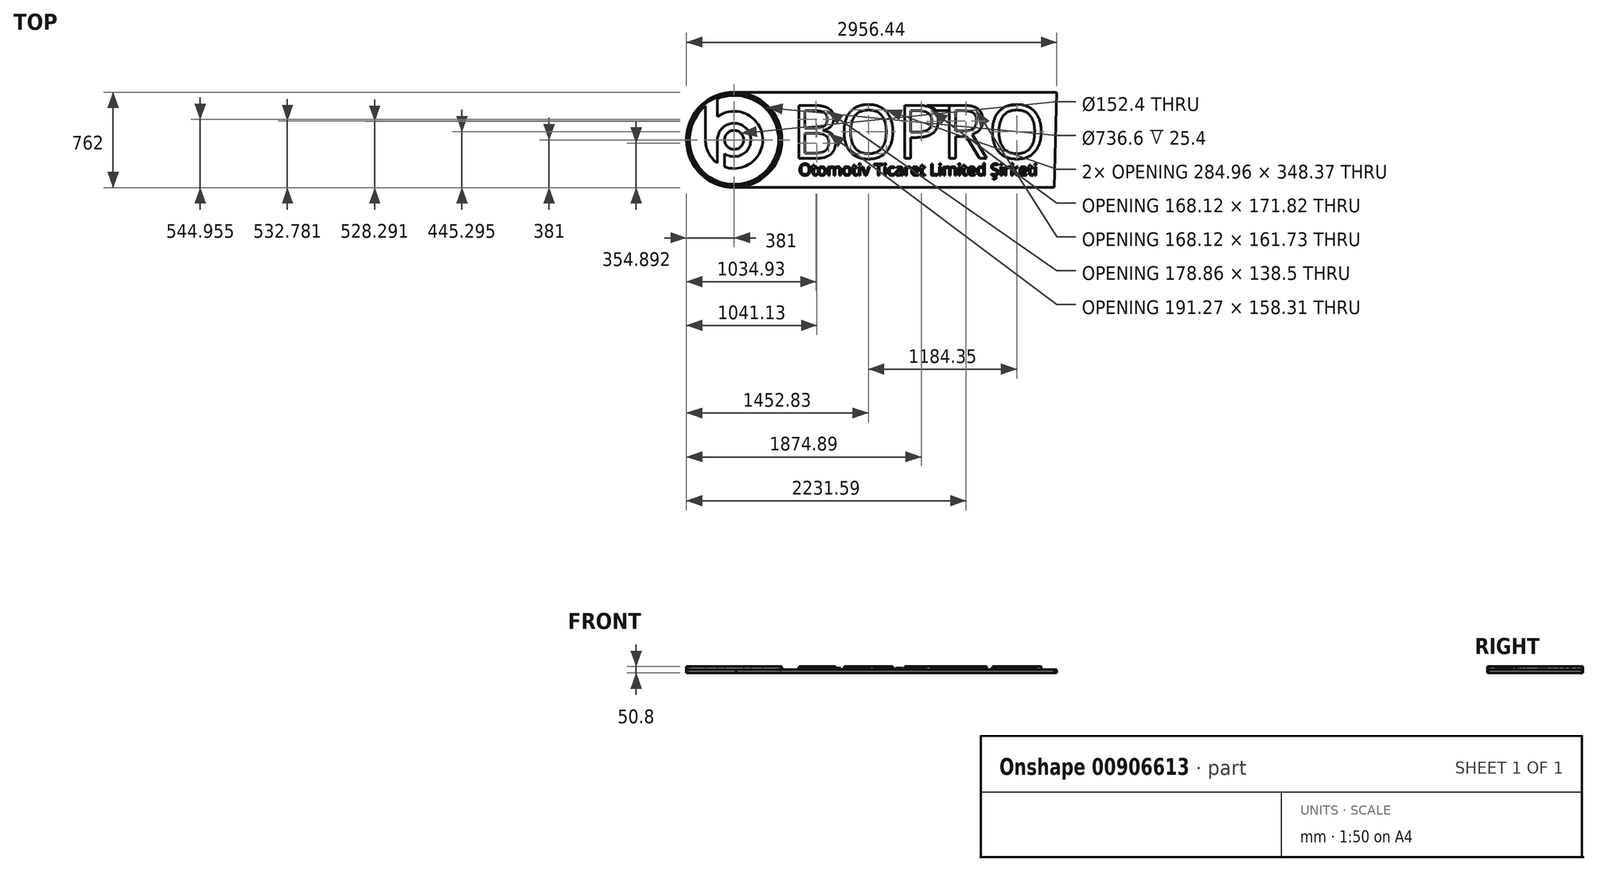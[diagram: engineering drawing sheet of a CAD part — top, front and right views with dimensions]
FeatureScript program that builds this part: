
annotation { "Feature Type Name" : "Feature", "Feature Type Description" : "" }
export const myFeature = defineFeature(function(context is Context, id is Id, definition is map)
    precondition{}
    {
        {
            var Q0;
            Q0=qCreatedBy(makeId("Top.planeOp"),FACE);
            var sketch = newSketch(context, id + "F0", { "sketchPlane" : qUnion([Q0])});
            skCircle(sketch, "E0", {"center": v(0, 0) * mm, "radius": 76.2 * mm});
            skArc(sketch, "E1", {"start": v(-76.2, -109.43) * mm, "mid": v(118.2, 61.73) * mm, "end": v(-133.35, 0) * mm});
            skArc(sketch, "E2", {"start": v(-228.6, 0) * mm, "mid": v(-203.4, -104.34) * mm, "end": v(-133.35, -185.68) * mm});
            skArc(sketch, "E3", {"start": v(-228.6, 272.38) * mm, "mid": v(183.23, -304.76) * mm, "end": v(-133.35, 329.65) * mm});
            skCircle(sketch, "E4", {"center": v(0, 0) * mm, "radius": 368.3 * mm});
            skCircle(sketch, "E5", {"center": v(0, 0) * mm, "radius": 381 * mm});
            skLineSegment(sketch, "E6", {"start": v(-76.2, -109.43) * mm, "end": v(-76.2, -215.53) * mm});
            skLineSegment(sketch, "E7", {"start": v(-133.35, 0) * mm, "end": v(-133.35, -185.68) * mm});
            skPoint(sketch, "E8.orphan", {"position": v(-76.2, 0) * mm});
            skLineSegment(sketch, "E9", {"start": v(-228.6, 0) * mm, "end": v(-228.6, 272.38) * mm});
            skLineSegment(sketch, "E10", {"start": v(-133.35, 185.68) * mm, "end": v(-133.35, 329.65) * mm});
            skArc(sketch, "E11.trimOffspring", {"start": v(-76.2, -215.53) * mm, "mid": v(226.32, 32.24) * mm, "end": v(-133.35, 185.68) * mm});
            skSolve(sketch);
        }
        {
            var Q0;
            Q0=makeQuery(id+"F0.imprint","IMPRINT",FACE,{"disambiguationData":[TD([[makeQuery(id+"F0.imprint","IMPRINT",EDGE,{"derivedFrom":sQuery(id+"F0.wireOp",EDGE,"E4")}),-1.0]])]});
            var Q1;
            Q1=makeQuery(id+"F0.imprint","IMPRINT",FACE,{"disambiguationData":[TD([[makeQuery(id+"F0.imprint","IMPRINT",EDGE,{"derivedFrom":sQuery(id+"F0.wireOp",EDGE,"E1")}),-1.0]])]});
            var Q2;
            Q2=makeQuery(id+"F0.imprint","IMPRINT",FACE,{"disambiguationData":[TD([[makeQuery(id+"F0.imprint","IMPRINT",EDGE,{"derivedFrom":sQuery(id+"F0.wireOp",EDGE,"E0")}),-1.0]])]});
            var Q3;
            Q3=makeQuery(id+"F0.imprint","IMPRINT",FACE,{"disambiguationData":[TD([[makeQuery(id+"F0.imprint","IMPRINT",EDGE,{"derivedFrom":sQuery(id+"F0.wireOp",EDGE,"E0")}),1.0]])]});
            extrude(context, id + "F1", {"entities" : qUnion([Q0, Q1, Q2, Q3]), "oppositeDirection" : true, "depth" : 25.4 * mm, "offsetDistance" : 25.4 * mm});
        }
        {
            var Q0;
            Q0=makeQuery(id+"F0.imprint","IMPRINT",FACE,{"disambiguationData":[TD([[makeQuery(id+"F0.imprint","IMPRINT",EDGE,{"derivedFrom":sQuery(id+"F0.wireOp",EDGE,"E4")}),-1.0]])]});
            var Q1;
            Q1=makeQuery(id+"F0.imprint","IMPRINT",FACE,{"disambiguationData":[TD([[makeQuery(id+"F0.imprint","IMPRINT",EDGE,{"derivedFrom":sQuery(id+"F0.wireOp",EDGE,"E0")}),-1.0]])]});
            extrude(context, id + "F2", {"entities" : qUnion([Q0, Q1]), "depth" : 25.4 * mm, "offsetDistance" : 25.4 * mm});
        }
        {
            var Q0;
            Q0=makeQuery(id+"F1.opExtrude","CAP_FACE",FACE,{"disambiguationData":[OSD([sQuery(id+"F0.wireOp",EDGE,"E5")])],"isStart":false});
            var sketch = newSketch(context, id + "F3", { "sketchPlane" : qUnion([Q0])});
            skCircle(sketch, "E12", {"center": v(0, 0) * mm, "radius": 368.3 * mm});
            skSolve(sketch);
        }
        {
            var Q0;
            Q0=makeQuery(id+"F3.imprint","IMPRINT",FACE,{"disambiguationData":[TD([[makeQuery(id+"F3.imprint","IMPRINT",EDGE,{"derivedFrom":sQuery(id+"F3.wireOp",EDGE,"E12")}),-1.0]])]});
            extrude(context, id + "F4", {"entities" : qUnion([Q0]), "operationType" : NewBodyOperationType.REMOVE, "oppositeDirection" : true, "depth" : 25.4 * mm, "offsetDistance" : 25.4 * mm});
        }
        {
            var Q0;
            Q0=makeQuery(id+"F1.opExtrude","CAP_FACE",FACE,{"disambiguationData":[OSD([sQuery(id+"F0.wireOp",EDGE,"E5")])],"isStart":true});
            var sketch = newSketch(context, id + "F5", { "sketchPlane" : qUnion([Q0])});
            skCircle(sketch, "E13.0", {"center": v(0, 0) * mm, "radius": 381 * mm});
            skLineSegment(sketch, "E14", {"start": v(-0.13, 381) * mm, "end": v(2575.44, 381) * mm});
            skLineSegment(sketch, "E15", {"start": v(14.68, -380.72) * mm, "end": v(2554.68, -380.72) * mm});
            skLineSegment(sketch, "E16", {"start": v(2575.44, 381) * mm, "end": v(2554.68, -380.72) * mm});
            skSolve(sketch);
        }
        {
            var Q0;
            Q0 = qSketchRegion(id + "F5", true);
            extrude(context, id + "F6", {"entities" : qUnion([Q0]), "oppositeDirection" : true, "depth" : 25.4 * mm, "offsetDistance" : 25.4 * mm});
        }
        {
            var Q0;
            Q0=makeQuery(id+"F6.opExtrude","CAP_FACE",FACE,{"disambiguationData":[OSD([sQuery(id+"F5.wireOp",EDGE,"E13.0"),sQuery(id+"F5.wireOp",EDGE,"E14"),sQuery(id+"F5.wireOp",EDGE,"E15"),sQuery(id+"F5.wireOp",EDGE,"E16")])],"isStart":true});
            var sketch = newSketch(context, id + "F7", { "sketchPlane" : qUnion([Q0])});
            skText(sketch, "E17", { "text": "BOPRO", "fontName": "OpenSans-Regular.ttf"});
            skCircle(sketch, "E18.0", {"center": v(0, 0) * mm, "radius": 381 * mm});
            skLineSegment(sketch, "E19.0.0", {"start": v(2575.44, 381) * mm, "end": v(0.13, 381) * mm});
            skArc(sketch, "E19.0.1", {"start": v(0.13, 381) * mm, "mid": v(-380.93, -7.27) * mm, "end": v(14.68, -380.72) * mm});
            skLineSegment(sketch, "E19.0.2", {"start": v(14.68, -380.72) * mm, "end": v(2554.68, -380.72) * mm});
            skLineSegment(sketch, "E19.0.3", {"start": v(2554.68, -380.72) * mm, "end": v(2575.44, 381) * mm});
            const initialGuessF7  = {"E17": [0.4572, -0.1472, 1, 0, 0.4266]};
            skSetInitialGuess(sketch, initialGuessF7);
            skSolve(sketch);
        }
        {
            var Q0;
            Q0=makeQuery(id+"F7.imprint","IMPRINT",FACE,{"disambiguationData":[TD([[makeQuery(id+"F7.imprint","IMPRINT",EDGE,{"derivedFrom":sQuery(id+"F7.wireOp",EDGE,"E17.sketch_text.stroke-0")}),-1.0]])]});
            var Q1;
            Q1=makeQuery(id+"F7.imprint","IMPRINT",FACE,{"disambiguationData":[TD([[makeQuery(id+"F7.imprint","IMPRINT",EDGE,{"derivedFrom":sQuery(id+"F7.wireOp",EDGE,"E17.sketch_text.stroke-25")}),-1.0]])]});
            var Q2;
            Q2=makeQuery(id+"F7.imprint","IMPRINT",FACE,{"disambiguationData":[TD([[makeQuery(id+"F7.imprint","IMPRINT",EDGE,{"derivedFrom":sQuery(id+"F7.wireOp",EDGE,"E17.sketch_text.stroke-41")}),-1.0]])]});
            var Q3;
            Q3=makeQuery(id+"F7.imprint","IMPRINT",FACE,{"disambiguationData":[TD([[makeQuery(id+"F7.imprint","IMPRINT",EDGE,{"derivedFrom":sQuery(id+"F7.wireOp",EDGE,"E17.sketch_text.stroke-56")}),-1.0]])]});
            var Q4;
            Q4=makeQuery(id+"F7.imprint","IMPRINT",FACE,{"disambiguationData":[TD([[makeQuery(id+"F7.imprint","IMPRINT",EDGE,{"derivedFrom":sQuery(id+"F7.wireOp",EDGE,"E17.sketch_text.stroke-74")}),-1.0]])]});
            extrude(context, id + "F8", {"entities" : qUnion([Q0, Q1, Q2, Q3, Q4]), "depth" : 25.4 * mm, "offsetDistance" : 25.4 * mm});
        }
        {
            var Q0;
            Q0=makeQuery(id+"F8.opExtrude","CAP_FACE",FACE,{"disambiguationData":[OSD([sQuery(id+"F7.wireOp",EDGE,"E17.sketch_text.stroke-56"),sQuery(id+"F7.wireOp",EDGE,"E17.sketch_text.stroke-57"),sQuery(id+"F7.wireOp",EDGE,"E17.sketch_text.stroke-58"),sQuery(id+"F7.wireOp",EDGE,"E17.sketch_text.stroke-59"),sQuery(id+"F7.wireOp",EDGE,"E17.sketch_text.stroke-60"),sQuery(id+"F7.wireOp",EDGE,"E17.sketch_text.stroke-61"),sQuery(id+"F7.wireOp",EDGE,"E17.sketch_text.stroke-62"),sQuery(id+"F7.wireOp",EDGE,"E17.sketch_text.stroke-63"),sQuery(id+"F7.wireOp",EDGE,"E17.sketch_text.stroke-64"),sQuery(id+"F7.wireOp",EDGE,"E17.sketch_text.stroke-65"),sQuery(id+"F7.wireOp",EDGE,"E17.sketch_text.stroke-66"),sQuery(id+"F7.wireOp",EDGE,"E17.sketch_text.stroke-67"),sQuery(id+"F7.wireOp",EDGE,"E17.sketch_text.stroke-68"),sQuery(id+"F7.wireOp",EDGE,"E17.sketch_text.stroke-69"),sQuery(id+"F7.wireOp",EDGE,"E17.sketch_text.stroke-70"),sQuery(id+"F7.wireOp",EDGE,"E17.sketch_text.stroke-71"),sQuery(id+"F7.wireOp",EDGE,"E17.sketch_text.stroke-72"),sQuery(id+"F7.wireOp",EDGE,"E17.sketch_text.stroke-73")])],"isStart":false});
            var sketch = newSketch(context, id + "F9", { "sketchPlane" : qUnion([Q0])});
            skLineSegment(sketch, "E20.0.1", {"start": v(1854.85, 28.7) * mm, "end": v(1957.25, -147.2) * mm});
            skLineSegment(sketch, "E20.0.2", {"start": v(1957.25, -147.2) * mm, "end": v(2015.38, -147.2) * mm});
            skLineSegment(sketch, "E20.0.3", {"start": v(2015.38, -147.2) * mm, "end": v(1900.5, 42.86) * mm});
            skFitSpline(sketch, "E20.0.4", {"points": [v(1900.5, 42.86) * mm, v(1985.57, 72.4) * mm, v(1985.57, 156.27) * mm]});
            skFitSpline(sketch, "E20.0.5", {"points": [v(1985.57, 156.27) * mm, v(1985.57, 216.17) * mm, v(1948.4, 245.98) * mm]});
            skFitSpline(sketch, "E20.0.6", {"points": [v(1948.4, 245.98) * mm, v(1911.23, 275.79) * mm, v(1833.38, 275.79) * mm]});
            skLineSegment(sketch, "E20.0.7", {"start": v(1833.38, 275.79) * mm, "end": v(1717.38, 275.79) * mm});
            skFitSpline(sketch, "E21.0.0", {"points": [v(1628.87, 152.57) * mm, v(1628.87, 275.79) * mm, v(1470.38, 275.79) * mm]});
            skLineSegment(sketch, "E21.0.1", {"start": v(1470.38, 275.79) * mm, "end": v(1360.67, 275.79) * mm});
            skLineSegment(sketch, "E21.0.2", {"start": v(1360.67, 275.79) * mm, "end": v(1360.67, -147.2) * mm});
            skLineSegment(sketch, "E21.0.3", {"start": v(1360.67, -147.2) * mm, "end": v(1409.83, -147.2) * mm});
            skLineSegment(sketch, "E21.0.4", {"start": v(1409.83, -147.2) * mm, "end": v(1409.83, 19.16) * mm});
            skLineSegment(sketch, "E21.0.5", {"start": v(1409.83, 19.16) * mm, "end": v(1459.64, 19.16) * mm});
            skFitSpline(sketch, "E21.0.6", {"points": [v(1459.64, 19.16) * mm, v(1541.2, 19.16) * mm, v(1585.03, 53.74) * mm]});
            skFitSpline(sketch, "E21.0.7", {"points": [v(1585.03, 53.74) * mm, v(1628.87, 88.32) * mm, v(1628.87, 152.57) * mm]});
            skLineSegment(sketch, "E22", {"start": v(1717.38, 275.79) * mm, "end": v(1540.02, 275.79) * mm});
            skLineSegment(sketch, "E23", {"start": v(1766.53, 232.65) * mm, "end": v(1612.47, 232.65) * mm});
            skFitSpline(sketch, "E24", {"points": [v(1540.02, 275.79) * mm, v(1579.9, 261.04) * mm, v(1612.47, 232.65) * mm], "startDerivative": vector(63.64, -12.57) * mm, "endDerivative": vector(28.33, -37.92) * mm});
            skLineSegment(sketch, "E25", {"start": v(1957.25, -147.2) * mm, "end": v(1830.28, 70.91) * mm});
            skPoint(sketch, "E20.0.10.end.orphan", {"position": v(1766.53, 28.7) * mm});
            skPoint(sketch, "E20.0.9.end.orphan", {"position": v(1766.53, -147.2) * mm});
            skPoint(sketch, "E20.0.9.start.orphan", {"position": v(1717.38, -147.2) * mm});
            skSolve(sketch);
        }
        {
            var Q0;
            {var subQ0=sQuery(id+"F9.wireOp",EDGE,"E22");Q0=makeQuery(id+"F9.imprint","IMPRINT",FACE,{"disambiguationData":[TD([[makeQuery(id+"F9.imprint","IMPRINT",EDGE,{"derivedFrom":subQ0}),1.0]])]});}
            extrude(context, id + "F10", {"entities" : qUnion([Q0]), "oppositeDirection" : true, "depth" : 25.4 * mm, "offsetDistance" : 25.4 * mm});
        }
        {
            var Q0;
            Q0=makeQuery(id+"F8.opExtrude","CAP_FACE",FACE,{"disambiguationData":[OSD([sQuery(id+"F7.wireOp",EDGE,"E17.sketch_text.stroke-56"),sQuery(id+"F7.wireOp",EDGE,"E17.sketch_text.stroke-57"),sQuery(id+"F7.wireOp",EDGE,"E17.sketch_text.stroke-58"),sQuery(id+"F7.wireOp",EDGE,"E17.sketch_text.stroke-59"),sQuery(id+"F7.wireOp",EDGE,"E17.sketch_text.stroke-60"),sQuery(id+"F7.wireOp",EDGE,"E17.sketch_text.stroke-61"),sQuery(id+"F7.wireOp",EDGE,"E17.sketch_text.stroke-62"),sQuery(id+"F7.wireOp",EDGE,"E17.sketch_text.stroke-63"),sQuery(id+"F7.wireOp",EDGE,"E17.sketch_text.stroke-64"),sQuery(id+"F7.wireOp",EDGE,"E17.sketch_text.stroke-65"),sQuery(id+"F7.wireOp",EDGE,"E17.sketch_text.stroke-66"),sQuery(id+"F7.wireOp",EDGE,"E17.sketch_text.stroke-67"),sQuery(id+"F7.wireOp",EDGE,"E17.sketch_text.stroke-68"),sQuery(id+"F7.wireOp",EDGE,"E17.sketch_text.stroke-69"),sQuery(id+"F7.wireOp",EDGE,"E17.sketch_text.stroke-70"),sQuery(id+"F7.wireOp",EDGE,"E17.sketch_text.stroke-71"),sQuery(id+"F7.wireOp",EDGE,"E17.sketch_text.stroke-72"),sQuery(id+"F7.wireOp",EDGE,"E17.sketch_text.stroke-73")])],"isStart":false});
            var sketch = newSketch(context, id + "F11", { "sketchPlane" : qUnion([Q0])});
            skLineSegment(sketch, "E26.0.0", {"start": v(1612.47, 232.65) * mm, "end": v(1717.38, 232.65) * mm});
            skLineSegment(sketch, "E26.0.1", {"start": v(1717.38, 232.65) * mm, "end": v(1717.38, 275.79) * mm});
            skLineSegment(sketch, "E26.0.2", {"start": v(1717.38, 275.79) * mm, "end": v(1540.02, 275.79) * mm});
            skFitSpline(sketch, "E26.0.3", {"points": [v(1540.02, 275.79) * mm, v(1550.59, 273.7) * mm, v(1580.87, 265.6) * mm, v(1607.73, 239) * mm, v(1612.47, 232.65) * mm]});
            skLineSegment(sketch, "E27.0.0", {"start": v(1766.53, 28.7) * mm, "end": v(1854.85, 28.7) * mm});
            skLineSegment(sketch, "E27.0.1", {"start": v(1854.85, 28.7) * mm, "end": v(1957.25, -147.2) * mm});
            skLineSegment(sketch, "E27.0.2", {"start": v(1957.25, -147.2) * mm, "end": v(2015.38, -147.2) * mm});
            skLineSegment(sketch, "E27.0.3", {"start": v(2015.38, -147.2) * mm, "end": v(1900.5, 42.86) * mm});
            skFitSpline(sketch, "E27.0.4", {"points": [v(1900.5, 42.86) * mm, v(1985.57, 72.4) * mm, v(1985.57, 156.27) * mm]});
            skFitSpline(sketch, "E27.0.5", {"points": [v(1985.57, 156.27) * mm, v(1985.57, 216.17) * mm, v(1948.4, 245.98) * mm]});
            skFitSpline(sketch, "E27.0.6", {"points": [v(1948.4, 245.98) * mm, v(1911.23, 275.79) * mm, v(1833.38, 275.79) * mm]});
            skLineSegment(sketch, "E27.0.7", {"start": v(1833.38, 275.79) * mm, "end": v(1717.38, 275.79) * mm});
            skLineSegment(sketch, "E27.0.8", {"start": v(1717.38, 275.79) * mm, "end": v(1717.38, -147.2) * mm});
            skLineSegment(sketch, "E27.0.9", {"start": v(1717.38, -147.2) * mm, "end": v(1766.53, -147.2) * mm});
            skLineSegment(sketch, "E27.0.10", {"start": v(1766.53, -147.2) * mm, "end": v(1766.53, 28.7) * mm});
            skLineSegment(sketch, "E28", {"start": v(1678.32, 232.65) * mm, "end": v(1805.1, 232.65) * mm});
            skLineSegment(sketch, "E29", {"start": v(1805.1, 232.65) * mm, "end": v(1766.53, 232.65) * mm});
            skLineSegment(sketch, "E30", {"start": v(1766.53, 232.65) * mm, "end": v(1766.53, 70.91) * mm});
            skLineSegment(sketch, "E31", {"start": v(1766.53, 70.91) * mm, "end": v(1830.5, 70.91) * mm});
            skLineSegment(sketch, "E32", {"start": v(1830.5, 70.91) * mm, "end": v(1854.85, 28.7) * mm});
            skLineSegment(sketch, "E33", {"start": v(1957.25, -147.2) * mm, "end": v(1830.5, 70.91) * mm});
            skLineSegment(sketch, "E34", {"start": v(1766.53, 28.7) * mm, "end": v(1766.53, -147.2) * mm});
            skSolve(sketch);
        }
        {
            var Q0;
            Q0=makeQuery(id+"F11.imprint","IMPRINT",FACE,{"disambiguationData":[TD([[makeQuery(id+"F11.imprint","IMPRINT",EDGE,{"derivedFrom":sQuery(id+"F11.wireOp",EDGE,"E27.0.0")}),-1.0]])]});
            extrude(context, id + "F12", {"entities" : qUnion([Q0]), "operationType" : NewBodyOperationType.REMOVE, "oppositeDirection" : true, "depth" : 25.4 * mm, "offsetDistance" : 25.4 * mm});
        }
        {
            var Q0;
            Q0=makeQuery(id+"F6.opExtrude","CAP_FACE",FACE,{"disambiguationData":[OSD([sQuery(id+"F5.wireOp",EDGE,"E13.0"),sQuery(id+"F5.wireOp",EDGE,"E14"),sQuery(id+"F5.wireOp",EDGE,"E15"),sQuery(id+"F5.wireOp",EDGE,"E16")])],"isStart":true});
            var sketch = newSketch(context, id + "F13", { "sketchPlane" : qUnion([Q0])});
            skText(sketch, "E35", { "text": "Otomotiv Ticaret Limited Şirketi", "fontName": "OpenSans-Regular.ttf"});
            const initialGuessF13  = {"E35": [0.51534, -0.28366, 1, 0, 0.09338]};
            skSetInitialGuess(sketch, initialGuessF13);
            skSolve(sketch);
        }
        {
            var Q0;
            Q0 = qSketchRegion(id + "F13", true);
            extrude(context, id + "F14", {"entities" : qUnion([Q0]), "operationType" : NewBodyOperationType.ADD, "depth" : 12.7 * mm, "offsetDistance" : 25.4 * mm});
        }
    });
